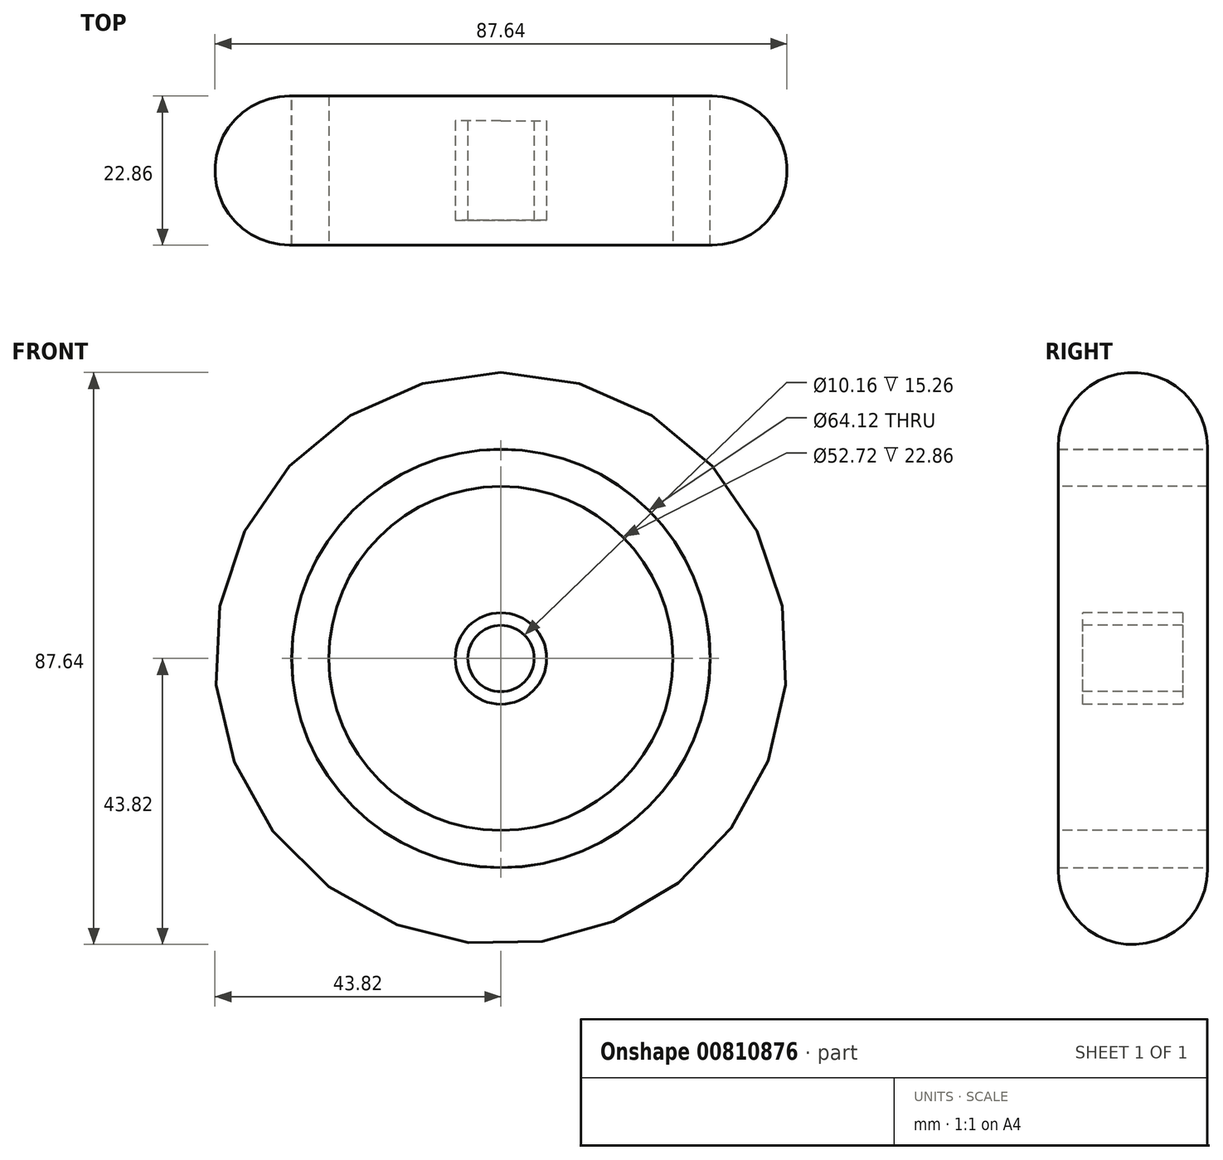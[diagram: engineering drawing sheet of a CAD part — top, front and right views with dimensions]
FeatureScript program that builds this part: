
annotation { "Feature Type Name" : "Feature", "Feature Type Description" : "" }
export const myFeature = defineFeature(function(context is Context, id is Id, definition is map)
    precondition{}
    {
        {
            var Q0;
            Q0=qCreatedBy(makeId("Front.planeOp"),FACE);
            var sketch = newSketch(context, id + "F0", { "sketchPlane" : qUnion([Q0])});
            skCircle(sketch, "E0", {"center": v(0, 0) * mm, "radius": 32.05 * mm});
            skSolve(sketch);
        }
        {
            var Q0;
            Q0 = qSketchRegion(id + "F0", true);
            extrude(context, id + "F1", {"entities" : qUnion([Q0]), "depth" : 22.86 * mm, "offsetDistance" : 25.4 * mm});
        }
        {
            var Q0;
            Q0=qCreatedBy(makeId("Right.planeOp"),FACE);
            var sketch = newSketch(context, id + "F2", { "sketchPlane" : qUnion([Q0])});
            skArc(sketch, "E1", {"start": v(0, 32.06) * mm, "mid": v(-11.43, 43.82) * mm, "end": v(-22.85, 32.06) * mm});
            skLineSegment(sketch, "E2", {"start": v(-22.85, 32.06) * mm, "end": v(0, 32.06) * mm});
            skSolve(sketch);
        }
        {
            var Q0;
            Q0 = qSketchRegion(id + "F2", true);
            var Q1;
            Q1=makeQuery(id+"F1.opExtrude","CAP_EDGE",EDGE,{"disambiguationData":[OSD([sQuery(id+"F0.wireOp",EDGE,"E0")])],"isStart":false});
            revolve(context, id + "F3", {"surfaceOperationType" : NewSurfaceOperationType.NEW, "entities" : qUnion([Q0]), "axis" : qUnion([Q1]), "revolveType" : RevolveType.FULL});
        }
        {
            var Q0;
            Q0=makeQuery(id+"F1.opExtrude","CAP_FACE",FACE,{"disambiguationData":[OSD([sQuery(id+"F0.wireOp",EDGE,"E0")])],"isStart":false});
            var sketch = newSketch(context, id + "F4", { "sketchPlane" : qUnion([Q0])});
            skCircle(sketch, "E3", {"center": v(0, 0) * mm, "radius": 26.36 * mm});
            skSolve(sketch);
        }
        {
            var Q0;
            Q0 = qSketchRegion(id + "F4", true);
            extrude(context, id + "F5", {"entities" : qUnion([Q0]), "operationType" : NewBodyOperationType.REMOVE, "oppositeDirection" : true, "depth" : 25.4 * mm, "offsetDistance" : 25.4 * mm});
        }
        {
            var Q0;
            Q0=makeQuery(id+"F1.opExtrude","CAP_FACE",FACE,{"disambiguationData":[OSD([sQuery(id+"F0.wireOp",EDGE,"E0")])],"isStart":false});
            var sketch = newSketch(context, id + "F6", { "sketchPlane" : qUnion([Q0])});
            skCircle(sketch, "E4", {"center": v(0, 0) * mm, "radius": 7 * mm});
            skSolve(sketch);
        }
        {
            var Q0;
            Q0 = qSketchRegion(id + "F6", true);
            var Q1;
            Q1=makeQuery(id+"F1.opExtrude","CAP_FACE",FACE,{"disambiguationData":[OSD([sQuery(id+"F0.wireOp",EDGE,"E0")])],"isStart":true});
            extrude(context, id + "F7", {"entities" : qUnion([Q0]), "endBound" : BoundingType.UP_TO_SURFACE, "oppositeDirection" : true, "depth" : 13.2 * mm, "endBoundEntityFace" : qUnion([Q1]), "offsetDistance" : 25.4 * mm});
        }
        {
            var Q0;
            Q0=makeQuery(id+"F7.opExtrude","CAP_FACE",FACE,{"disambiguationData":[OSD([sQuery(id+"F6.wireOp",EDGE,"E4")])],"isStart":true});
            var sketch = newSketch(context, id + "F8", { "sketchPlane" : qUnion([Q0])});
            skLineSegment(sketch, "E5", {"start": v(-2.83, 6.41) * mm, "end": v(-7.85, 25.15) * mm});
            skLineSegment(sketch, "E6", {"start": v(2.78, 6.43) * mm, "end": v(8.56, 24.99) * mm});
            skLineSegment(sketch, "E7", {"start": v(6.71, 2.01) * mm, "end": v(24.97, 8.54) * mm});
            skLineSegment(sketch, "E8", {"start": v(6.15, -3.36) * mm, "end": v(25.04, -8.53) * mm});
            skLineSegment(sketch, "E9", {"start": v(-2.83, -6.41) * mm, "end": v(-7.85, -25.4) * mm});
            skLineSegment(sketch, "E10", {"start": v(2.78, -6.43) * mm, "end": v(8.56, -25.26) * mm});
            skLineSegment(sketch, "E11", {"start": v(-6.71, 2.01) * mm, "end": v(-25.4, 8.54) * mm});
            skLineSegment(sketch, "E12", {"start": v(-6.15, -3.36) * mm, "end": v(-24.91, -8.53) * mm});
            skArc(sketch, "E13", {"start": v(8.56, 24.99) * mm, "mid": v(0.37, 26.5) * mm, "end": v(-7.85, 25.15) * mm});
            skArc(sketch, "E14", {"start": v(25.04, -8.53) * mm, "mid": v(26.38, 0) * mm, "end": v(24.97, 8.54) * mm});
            skArc(sketch, "E15", {"start": v(-7.85, -25.4) * mm, "mid": v(0.36, -26.7) * mm, "end": v(8.56, -25.26) * mm});
            skArc(sketch, "E16", {"start": v(-25.4, 8.54) * mm, "mid": v(-26.66, -0.04) * mm, "end": v(-24.91, -8.53) * mm});
            skCircle(sketch, "E17", {"center": v(0, 0) * mm, "radius": 7 * mm});
            skSolve(sketch);
        }
        {
            var Q0;
            Q0 = qSketchRegion(id + "F8", true);
            var Q1;
            Q1=makeQuery(id+"F1.opExtrude","CAP_FACE",FACE,{"disambiguationData":[OSD([sQuery(id+"F0.wireOp",EDGE,"E0")])],"isStart":true});
            extrude(context, id + "F9", {"entities" : qUnion([Q0]), "operationType" : NewBodyOperationType.ADD, "endBound" : BoundingType.UP_TO_SURFACE, "oppositeDirection" : true, "depth" : 25.4 * mm, "endBoundEntityFace" : qUnion([Q1]), "offsetDistance" : 25.4 * mm});
        }
        {
            var Q0;
            Q0=makeQuery(id+"F9.boolean.opBoolean","MERGE",FACE,{"derivedFrom":[makeQuery(id+"F1.opExtrude","CAP_FACE",FACE,{"disambiguationData":[OSD([sQuery(id+"F0.wireOp",EDGE,"E0")])],"isStart":false}),makeQuery(id+"F9.opExtrude","CAP_FACE",FACE,{"disambiguationData":[OSD([sQuery(id+"F8.wireOp",EDGE,"E5"),sQuery(id+"F8.wireOp",EDGE,"E6"),sQuery(id+"F8.wireOp",EDGE,"E7"),sQuery(id+"F8.wireOp",EDGE,"E8"),sQuery(id+"F8.wireOp",EDGE,"E9"),sQuery(id+"F8.wireOp",EDGE,"E10"),sQuery(id+"F8.wireOp",EDGE,"E11"),sQuery(id+"F8.wireOp",EDGE,"E12"),sQuery(id+"F8.wireOp",EDGE,"E13"),sQuery(id+"F8.wireOp",EDGE,"E14"),sQuery(id+"F8.wireOp",EDGE,"E15"),sQuery(id+"F8.wireOp",EDGE,"E16"),sQuery(id+"F8.wireOp",EDGE,"E17")])],"isStart":true})]});
            var sketch = newSketch(context, id + "F10", { "sketchPlane" : qUnion([Q0])});
            skLineSegment(sketch, "E18", {"start": v(-3.03, 24.1) * mm, "end": v(-0.99, 9.26) * mm});
            skLineSegment(sketch, "E19", {"start": v(-0.99, 9.26) * mm, "end": v(1.46, 9.26) * mm});
            skLineSegment(sketch, "E20", {"start": v(3.5, 24.1) * mm, "end": v(1.46, 9.26) * mm});
            skArc(sketch, "E21", {"start": v(3.5, 24.1) * mm, "mid": v(0.23, 24.9) * mm, "end": v(-3.03, 24.1) * mm});
            skArc(sketch, "E22.1.0", {"start": v(24.14, -3.18) * mm, "mid": v(24.9, 0.1) * mm, "end": v(24.05, 3.35) * mm});
            skLineSegment(sketch, "E22.1.1", {"start": v(24.14, -3.18) * mm, "end": v(9.28, -1.34) * mm});
            skLineSegment(sketch, "E22.1.2", {"start": v(9.25, 1.11) * mm, "end": v(9.28, -1.34) * mm});
            skLineSegment(sketch, "E22.1.3", {"start": v(24.05, 3.35) * mm, "end": v(9.25, 1.11) * mm});
            skArc(sketch, "E22.2.0", {"start": v(-2.86, -24.18) * mm, "mid": v(0.43, -24.9) * mm, "end": v(3.67, -24) * mm});
            skLineSegment(sketch, "E22.2.1", {"start": v(-2.86, -24.18) * mm, "end": v(-1.22, -9.3) * mm});
            skLineSegment(sketch, "E22.2.2", {"start": v(1.23, -9.23) * mm, "end": v(-1.22, -9.3) * mm});
            skLineSegment(sketch, "E22.2.3", {"start": v(3.67, -24) * mm, "end": v(1.23, -9.23) * mm});
            skArc(sketch, "E22.3.0", {"start": v(-24.21, 2.54) * mm, "mid": v(-24.88, -0.76) * mm, "end": v(-23.95, -3.99) * mm});
            skLineSegment(sketch, "E22.3.1", {"start": v(-24.21, 2.54) * mm, "end": v(-9.31, 1.1) * mm});
            skLineSegment(sketch, "E22.3.2", {"start": v(-9.21, -1.36) * mm, "end": v(-9.31, 1.1) * mm});
            skLineSegment(sketch, "E22.3.3", {"start": v(-23.95, -3.99) * mm, "end": v(-9.21, -1.36) * mm});
            skPoint(sketch, "E22.center", {"position": v(0, 0) * mm});
            skLineSegment(sketch, "E22.anchor1", {"start": v(0, 0) * mm, "end": v(0.23, 17.84) * mm, "construction": true});
            skLineSegment(sketch, "E22.anchor2", {"start": v(0, 0) * mm, "end": v(-17.83, -0.48) * mm, "construction": true});
            skSolve(sketch);
        }
        {
            var Q0;
            Q0 = qSketchRegion(id + "F10", true);
            extrude(context, id + "F11", {"entities" : qUnion([Q0]), "operationType" : NewBodyOperationType.REMOVE, "oppositeDirection" : true, "depth" : 25.4 * mm, "offsetDistance" : 25.4 * mm});
        }
        {
            var Q0;
            Q0=makeQuery(id+"F7.opExtrude","SWEPT_BODY",BODY,{"disambiguationData":[OSD([sQuery(id+"F6.wireOp",EDGE,"E4")])]});
            var Q1;
            Q1=makeQuery(id+"F1.opExtrude","SWEPT_BODY",BODY,{"disambiguationData":[OSD([sQuery(id+"F0.wireOp",EDGE,"E0")])]});
            booleanBodies(context, id + "F12", {"operationType" : BooleanOperationType.UNION, "tools" : qUnion([Q0, Q1])});
        }
        {
            var Q0;
            Q0=makeQuery(id+"F12.opBoolean","MERGE",FACE,{"derivedFrom":[makeQuery(id+"F7.opExtrude","CAP_FACE",FACE,{"disambiguationData":[OSD([sQuery(id+"F6.wireOp",EDGE,"E4")])],"isStart":true}),makeQuery(id+"F9.boolean.opBoolean","MERGE",FACE,{"derivedFrom":[makeQuery(id+"F1.opExtrude","CAP_FACE",FACE,{"disambiguationData":[OSD([sQuery(id+"F0.wireOp",EDGE,"E0")])],"isStart":false}),makeQuery(id+"F9.opExtrude","CAP_FACE",FACE,{"disambiguationData":[OSD([sQuery(id+"F8.wireOp",EDGE,"E5"),sQuery(id+"F8.wireOp",EDGE,"E6"),sQuery(id+"F8.wireOp",EDGE,"E7"),sQuery(id+"F8.wireOp",EDGE,"E8"),sQuery(id+"F8.wireOp",EDGE,"E9"),sQuery(id+"F8.wireOp",EDGE,"E10"),sQuery(id+"F8.wireOp",EDGE,"E11"),sQuery(id+"F8.wireOp",EDGE,"E12"),sQuery(id+"F8.wireOp",EDGE,"E13"),sQuery(id+"F8.wireOp",EDGE,"E14"),sQuery(id+"F8.wireOp",EDGE,"E15"),sQuery(id+"F8.wireOp",EDGE,"E16"),sQuery(id+"F8.wireOp",EDGE,"E17")])],"isStart":true})]})]});
            var sketch = newSketch(context, id + "F13", { "sketchPlane" : qUnion([Q0])});
            skCircle(sketch, "E23", {"center": v(0, 0) * mm, "radius": 5.08 * mm});
            skSolve(sketch);
        }
        {
            var Q0;
            Q0 = qSketchRegion(id + "F13", true);
            extrude(context, id + "F14", {"entities" : qUnion([Q0]), "operationType" : NewBodyOperationType.REMOVE, "oppositeDirection" : true, "depth" : 25.4 * mm, "offsetDistance" : 25.4 * mm});
        }
        {
            var Q0;
            Q0=makeQuery(id+"F12.opBoolean","MERGE",FACE,{"derivedFrom":[makeQuery(id+"F7.opExtrude","CAP_FACE",FACE,{"disambiguationData":[OSD([sQuery(id+"F6.wireOp",EDGE,"E4")])],"isStart":true}),makeQuery(id+"F9.boolean.opBoolean","MERGE",FACE,{"derivedFrom":[makeQuery(id+"F1.opExtrude","CAP_FACE",FACE,{"disambiguationData":[OSD([sQuery(id+"F0.wireOp",EDGE,"E0")])],"isStart":false}),makeQuery(id+"F9.opExtrude","CAP_FACE",FACE,{"disambiguationData":[OSD([sQuery(id+"F8.wireOp",EDGE,"E5"),sQuery(id+"F8.wireOp",EDGE,"E6"),sQuery(id+"F8.wireOp",EDGE,"E7"),sQuery(id+"F8.wireOp",EDGE,"E8"),sQuery(id+"F8.wireOp",EDGE,"E9"),sQuery(id+"F8.wireOp",EDGE,"E10"),sQuery(id+"F8.wireOp",EDGE,"E11"),sQuery(id+"F8.wireOp",EDGE,"E12"),sQuery(id+"F8.wireOp",EDGE,"E13"),sQuery(id+"F8.wireOp",EDGE,"E14"),sQuery(id+"F8.wireOp",EDGE,"E15"),sQuery(id+"F8.wireOp",EDGE,"E16"),sQuery(id+"F8.wireOp",EDGE,"E17")])],"isStart":true})]})]});
            var sketch = newSketch(context, id + "F15", { "sketchPlane" : qUnion([Q0])});
            skCircle(sketch, "E24", {"center": v(0, 0) * mm, "radius": 26.36 * mm});
            skSolve(sketch);
        }
        {
            var Q0;
            Q0 = qSketchRegion(id + "F15", true);
            extrude(context, id + "F16", {"entities" : qUnion([Q0]), "operationType" : NewBodyOperationType.REMOVE, "oppositeDirection" : true, "depth" : 3.8 * mm, "offsetDistance" : 25.4 * mm});
        }
        {
            var Q0;
            {var subQ0=sQuery(id+"F0.wireOp",EDGE,"E0");Q0=makeQuery(id+"F12.opBoolean","MERGE",FACE,{"derivedFrom":[makeQuery(id+"F7.opExtrude","CAP_FACE",FACE,{"disambiguationData":[OSD([subQ0])],"isStart":false}),makeQuery(id+"F9.boolean.opBoolean","MERGE",FACE,{"derivedFrom":[makeQuery(id+"F1.opExtrude","CAP_FACE",FACE,{"disambiguationData":[OSD([subQ0])],"isStart":true}),makeQuery(id+"F9.opExtrude","CAP_FACE",FACE,{"disambiguationData":[OSD([subQ0])],"isStart":false})]})]});}
            var sketch = newSketch(context, id + "F17", { "sketchPlane" : qUnion([Q0])});
            skCircle(sketch, "E25", {"center": v(0, 0) * mm, "radius": 26.36 * mm});
            skSolve(sketch);
        }
        {
            var Q0;
            Q0 = qSketchRegion(id + "F17", true);
            extrude(context, id + "F18", {"entities" : qUnion([Q0]), "operationType" : NewBodyOperationType.REMOVE, "oppositeDirection" : true, "depth" : 3.8 * mm, "offsetDistance" : 25.4 * mm});
        }
    });
